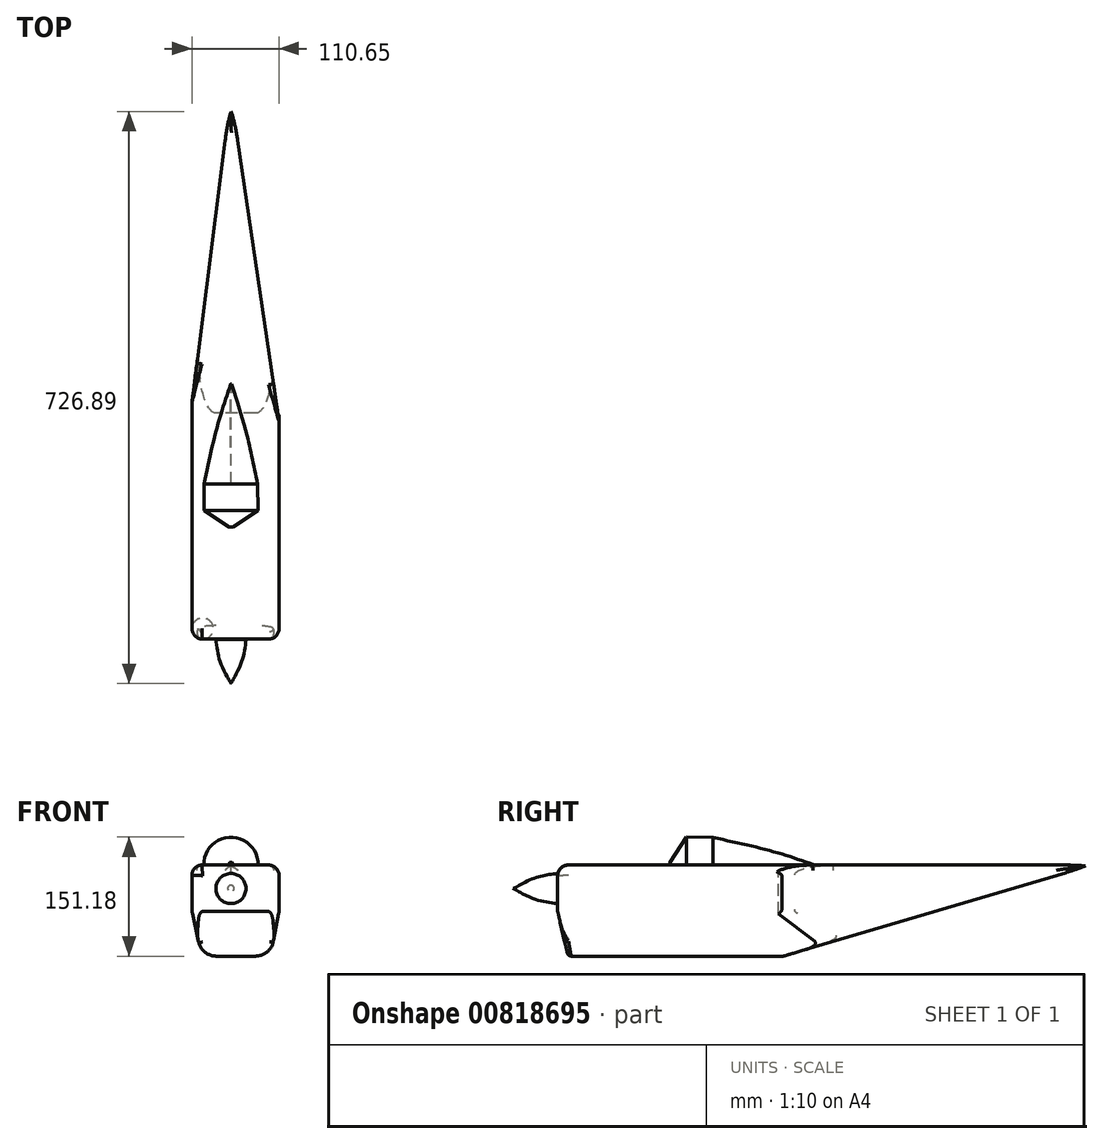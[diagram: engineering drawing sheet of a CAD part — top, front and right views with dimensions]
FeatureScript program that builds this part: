
annotation { "Feature Type Name" : "Feature", "Feature Type Description" : "" }
export const myFeature = defineFeature(function(context is Context, id is Id, definition is map)
    precondition{}
    {
        {
            var Q0;
            Q0=qCreatedBy(makeId("Front.planeOp"),FACE);
            var sketch = newSketch(context, id + "F0", { "sketchPlane" : qUnion([Q0])});
            skLineSegment(sketch, "E0.bottom", {"start": v(-36.8, 41.62) * mm, "end": v(48.49, 41.62) * mm});
            skPoint(sketch, "E1.visualSharp", {"position": v(-49.5, 41.62) * mm});
            skArc(sketch, "E1.filletArc", {"start": v(-36.8, 41.62) * mm, "mid": v(-45.78, 37.9) * mm, "end": v(-49.5, 28.92) * mm});
            skPoint(sketch, "E2.visualSharp", {"position": v(61.15, 41.62) * mm});
            skArc(sketch, "E2.filletArc", {"start": v(61.15, 29.9) * mm, "mid": v(57.11, 38.24) * mm, "end": v(48.49, 41.62) * mm});
            skLineSegment(sketch, "E3", {"start": v(-49.5, 28.92) * mm, "end": v(-49.5, -14.97) * mm});
            skLineSegment(sketch, "E4", {"start": v(61.15, 29.9) * mm, "end": v(61.15, -15.21) * mm});
            skLineSegment(sketch, "E5", {"start": v(-48.98, -19.8) * mm, "end": v(-41.15, -56.04) * mm});
            skLineSegment(sketch, "E6", {"start": v(-18.8, -74.07) * mm, "end": v(31.3, -74.07) * mm});
            skLineSegment(sketch, "E7", {"start": v(60.73, -19.56) * mm, "end": v(53.75, -55.56) * mm});
            skPoint(sketch, "E8.visualSharp", {"position": v(-49.5, -17.4) * mm});
            skArc(sketch, "E8.filletArc", {"start": v(-49.5, -14.97) * mm, "mid": v(-49.37, -17.4) * mm, "end": v(-48.98, -19.8) * mm});
            skPoint(sketch, "E9.visualSharp", {"position": v(61.15, -17.4) * mm});
            skArc(sketch, "E9.filletArc", {"start": v(60.73, -19.56) * mm, "mid": v(61.04, -17.4) * mm, "end": v(61.15, -15.21) * mm});
            skPoint(sketch, "E10.visualSharp", {"position": v(-37.26, -74.07) * mm});
            skArc(sketch, "E10.filletArc", {"start": v(-41.15, -56.04) * mm, "mid": v(-33.16, -69) * mm, "end": v(-18.8, -74.07) * mm});
            skPoint(sketch, "E11.visualSharp", {"position": v(50.16, -74.07) * mm});
            skArc(sketch, "E11.filletArc", {"start": v(31.3, -74.07) * mm, "mid": v(45.85, -68.85) * mm, "end": v(53.75, -55.56) * mm});
            skSolve(sketch);
        }
        {
            var Q0;
            Q0=makeQuery(id+"F0.imprint","IMPRINT",FACE,{"disambiguationData":[TD([[makeQuery(id+"F0.imprint","IMPRINT",EDGE,{"derivedFrom":sQuery(id+"F0.wireOp",EDGE,"E0.bottom")}),-1.0]])]});
            extrude(context, id + "F1", {"entities" : qUnion([Q0]), "depth" : 197.36 * mm, "offsetDistance" : 25.4 * mm});
        }
        {
            var Q0;
            Q0=qCreatedBy(makeId("Right.planeOp"),FACE);
            var sketch = newSketch(context, id + "F2", { "sketchPlane" : qUnion([Q0])});
            skLineSegment(sketch, "E12", {"start": v(-198.25, -13.52) * mm, "end": v(-183.44, -77.59) * mm});
            skLineSegment(sketch, "E13", {"start": v(-183.44, -77.59) * mm, "end": v(-211.91, -77.59) * mm});
            skLineSegment(sketch, "E14", {"start": v(-211.91, -77.59) * mm, "end": v(-198.25, -13.52) * mm});
            skSolve(sketch);
        }
        {
            var Q0;
            Q0 = qSketchRegion(id + "F2", true);
            extrude(context, id + "F3", {"entities" : qUnion([Q0]), "operationType" : NewBodyOperationType.REMOVE, "endBound" : BoundingType.SYMMETRIC, "oppositeDirection" : true, "depth" : 143.26 * mm, "offsetDistance" : 25.4 * mm});
        }
        {
            var Q0;
            Q0=makeQuery(id+"F1.opExtrude","CAP_EDGE",EDGE,{"disambiguationData":[OSD([sQuery(id+"F0.wireOp",EDGE,"E0.bottom")])],"isStart":false});
            var Q1;
            Q1=makeQuery(id+"F1.opExtrude","CAP_EDGE",EDGE,{"disambiguationData":[OSD([sQuery(id+"F0.wireOp",EDGE,"E1.filletArc")])],"isStart":false});
            fillet(context, id + "F4", {"entities" : qUnion([Q0, Q1]), "radius" : 13.5 * mm, "tangentPropagation" : true, "allowEdgeOverflow" : false});
        }
        {
            var Q0;
            Q0=makeQuery(id+"F1.opExtrude","CAP_EDGE",EDGE,{"disambiguationData":[OSD([sQuery(id+"F0.wireOp",EDGE,"E4")])],"isStart":false});
            fillet(context, id + "F5", {"entities" : qUnion([Q0]), "radius" : 13.5 * mm, "tangentPropagation" : true, "allowEdgeOverflow" : false});
        }
        {
            var Q0;
            Q0=makeQuery(id+"F3.boolean.opBoolean","INTERSECT",EDGE,{"derivedFrom":[makeQuery(id+"F1.opExtrude","SWEPT_FACE",FACE,{"disambiguationData":[OSD([sQuery(id+"F0.wireOp",EDGE,"E6")])]}),makeQuery(id+"F3.opExtrude","SWEPT_FACE",FACE,{"disambiguationData":[OSD([sQuery(id+"F2.wireOp",EDGE,"E12")])]})]});
            fillet(context, id + "F6", {"entities" : qUnion([Q0]), "radius" : 5.08 * mm, "tangentPropagation" : true, "allowEdgeOverflow" : false});
        }
        {
            var Q0;
            Q0=qCreatedBy(makeId("Right.planeOp"),FACE);
            var sketch = newSketch(context, id + "F7", { "sketchPlane" : qUnion([Q0])});
            skFitSpline(sketch, "E15", {"points": [v(-197.64, 30.82) * mm, v(-231.23, 23.4) * mm, v(-253.86, 11.73) * mm, v(-254.21, 11.73) * mm], "startDerivative": vector(-64.18, -7.39) * mm, "endDerivative": vector(-4.4, 1.73) * mm});
            skLineSegment(sketch, "E16", {"start": v(-253.86, 11.73) * mm, "end": v(-197.28, 11.73) * mm});
            skLineSegment(sketch, "E17", {"start": v(-197.28, 11.73) * mm, "end": v(-197.64, 30.82) * mm});
            skSolve(sketch);
        }
        {
            var Q0;
            {var subQ2=sQuery(id+"F7.wireOp",EDGE,"E16");Q0=makeQuery(id+"F7.imprint","IMPRINT",FACE,{"disambiguationData":[TD([[makeQuery(id+"F7.imprint","IMPRINT",EDGE,{"derivedFrom":subQ2}),1.0]])]});}
            var Q1;
            Q1=sQuery(id+"F7.wireOp",EDGE,"E16");
            revolve(context, id + "F8", {"operationType" : NewBodyOperationType.ADD, "surfaceOperationType" : NewSurfaceOperationType.NEW, "entities" : qUnion([Q0]), "axis" : qUnion([Q1]), "revolveType" : RevolveType.FULL});
        }
        {
            var Q0;
            Q0=qCreatedBy(makeId("Right.planeOp"),FACE);
            var sketch = newSketch(context, id + "F9", { "sketchPlane" : qUnion([Q0])});
            skFitSpline(sketch, "E18", {"points": [v(-230.36, 22.97) * mm, v(-230.36, 83.18) * mm, v(-212.3, 158.02) * mm, v(-213.16, 160.6) * mm], "startDerivative": vector(-15.1, 123.32) * mm, "endDerivative": vector(-14.55, 16.84) * mm});
            skLineSegment(sketch, "E19", {"start": v(-221.76, 21.25) * mm, "end": v(-200.25, 158.88) * mm});
            skSolve(sketch);
        }
        {
            var Q0;
            Q0=sQuery(id+"F9.wireOp",EDGE,"E18");
            var Q1;
            Q1=sQuery(id+"F9.wireOp",EDGE,"E19");
            revolve(context, id + "F10", {"bodyType" : ToolBodyType.SURFACE, "surfaceOperationType" : NewSurfaceOperationType.NEW, "surfaceEntities" : qUnion([Q0]), "axis" : qUnion([Q1]), "revolveType" : RevolveType.SYMMETRIC, "angle" : 64.7 * degree});
        }
        {
            var Q0;
            Q0=makeQuery(id+"F10.opRevolve","SWEPT_BODY",BODY,{"disambiguationData":[OSD([sQuery(id+"F9.wireOp",EDGE,"E18")])]});
            var Q1;
            Q1=makeQuery(id+"F8.opRevolve","SWEPT_FACE",FACE,{"disambiguationData":[OSD([sQuery(id+"F7.wireOp",EDGE,"E15")])]});
            circularPattern(context, id + "F11", {"entities" : qUnion([Q0]), "axis" : qUnion([Q1]), "angle" : 360 * degree, "instanceCount" : 3, "equalSpace" : true});
        }
        {
            var Q0;
            Q0=makeQuery(id+"F1.opExtrude","CAP_FACE",FACE,{"disambiguationData":[OSD([sQuery(id+"F0.wireOp",EDGE,"E0.bottom"),sQuery(id+"F0.wireOp",EDGE,"E1.filletArc"),sQuery(id+"F0.wireOp",EDGE,"E2.filletArc"),sQuery(id+"F0.wireOp",EDGE,"E3"),sQuery(id+"F0.wireOp",EDGE,"E4"),sQuery(id+"F0.wireOp",EDGE,"E5"),sQuery(id+"F0.wireOp",EDGE,"E6"),sQuery(id+"F0.wireOp",EDGE,"E7"),sQuery(id+"F0.wireOp",EDGE,"E8.filletArc"),sQuery(id+"F0.wireOp",EDGE,"E9.filletArc"),sQuery(id+"F0.wireOp",EDGE,"E10.filletArc"),sQuery(id+"F0.wireOp",EDGE,"E11.filletArc")])],"isStart":true});
            extrude(context, id + "F12", {"entities" : qUnion([Q0]), "operationType" : NewBodyOperationType.ADD, "depth" : 487.68 * mm, "offsetDistance" : 25.4 * mm});
        }
        {
            var Q0;
            Q0=qCreatedBy(makeId("Right.planeOp"),FACE);
            var sketch = newSketch(context, id + "F13", { "sketchPlane" : qUnion([Q0])});
            skLineSegment(sketch, "E20", {"start": v(487.34, 43.68) * mm, "end": v(84.62, -75.55) * mm});
            skLineSegment(sketch, "E21", {"start": v(84.62, -75.55) * mm, "end": v(96.3, -139.76) * mm});
            skLineSegment(sketch, "E22", {"start": v(-92.85, -139.76) * mm, "end": v(-114.72, -139.76) * mm});
            skLineSegment(sketch, "E23", {"start": v(96.3, -139.76) * mm, "end": v(500.84, -115.19) * mm});
            skLineSegment(sketch, "E24", {"start": v(508.98, -115.19) * mm, "end": v(508.98, 90.1) * mm});
            skLineSegment(sketch, "E25", {"start": v(487.34, 43.68) * mm, "end": v(508.98, 90.1) * mm});
            skLineSegment(sketch, "E26", {"start": v(508.98, 93.48) * mm, "end": v(500.84, -115.19) * mm});
            skLineSegment(sketch, "E27", {"start": v(508.98, -115.19) * mm, "end": v(500.84, -115.19) * mm});
            skSolve(sketch);
        }
        {
            var Q0;
            Q0 = qSketchRegion(id + "F13", true);
            extrude(context, id + "F14", {"entities" : qUnion([Q0]), "operationType" : NewBodyOperationType.REMOVE, "endBound" : BoundingType.SYMMETRIC, "depth" : 284.48 * mm, "offsetDistance" : 25.4 * mm});
        }
        {
            var Q0;
            Q0=qCreatedBy(makeId("Top.planeOp"),FACE);
            var sketch = newSketch(context, id + "F15", { "sketchPlane" : qUnion([Q0])});
            skLineSegment(sketch, "E28", {"start": v(-51.82, 85.84) * mm, "end": v(0, 494.02) * mm});
            skLineSegment(sketch, "E29", {"start": v(0, 494.02) * mm, "end": v(60.58, 82.88) * mm});
            skLineSegment(sketch, "E30", {"start": v(60.58, 82.88) * mm, "end": v(116.78, 511.76) * mm});
            skLineSegment(sketch, "E31", {"start": v(116.78, 511.76) * mm, "end": v(-122.8, 494.02) * mm});
            skLineSegment(sketch, "E32", {"start": v(-122.8, 494.02) * mm, "end": v(-51.82, 85.84) * mm});
            skSolve(sketch);
        }
        {
            var Q0;
            Q0 = qSketchRegion(id + "F15", true);
            extrude(context, id + "F16", {"entities" : qUnion([Q0]), "operationType" : NewBodyOperationType.REMOVE, "endBound" : BoundingType.SYMMETRIC, "oppositeDirection" : true, "depth" : 558.8 * mm, "offsetDistance" : 25.4 * mm});
        }
        {
            var Q0;
            {var subQ0=sQuery(id+"F0.wireOp",EDGE,"E0.bottom");Q0=makeQuery(id+"F16.boolean.opBoolean","INTERSECT",EDGE,{"derivedFrom":[makeQuery(id+"F12.boolean.opBoolean","MERGE",FACE,{"derivedFrom":[makeQuery(id+"F1.opExtrude","SWEPT_FACE",FACE,{"disambiguationData":[OSD([subQ0])]}),makeQuery(id+"F12.opExtrude","SWEPT_FACE",FACE,{"disambiguationData":[OSD([subQ0])]})]}),makeQuery(id+"F16.opExtrude","SWEPT_FACE",FACE,{"disambiguationData":[OSD([sQuery(id+"F15.wireOp",EDGE,"E28")])]})]});}
            var Q1;
            {var subQ0=sQuery(id+"F0.wireOp",EDGE,"E0.bottom");Q1=makeQuery(id+"F16.boolean.opBoolean","INTERSECT",EDGE,{"derivedFrom":[makeQuery(id+"F12.boolean.opBoolean","MERGE",FACE,{"derivedFrom":[makeQuery(id+"F1.opExtrude","SWEPT_FACE",FACE,{"disambiguationData":[OSD([subQ0])]}),makeQuery(id+"F12.opExtrude","SWEPT_FACE",FACE,{"disambiguationData":[OSD([subQ0])]})]}),makeQuery(id+"F16.opExtrude","SWEPT_FACE",FACE,{"disambiguationData":[OSD([sQuery(id+"F15.wireOp",EDGE,"E29")])]})]});}
            var Q2;
            Q2=makeQuery(id+"F16.boolean.opBoolean","INTERSECT",EDGE,{"derivedFrom":[makeQuery(id+"F14.boolean.opBoolean","COPY",FACE,{"derivedFrom":makeQuery(id+"F14.opExtrude","SWEPT_FACE",FACE,{"disambiguationData":[OSD([sQuery(id+"F13.wireOp",EDGE,"E20")])]})}),makeQuery(id+"F16.opExtrude","SWEPT_FACE",FACE,{"disambiguationData":[OSD([sQuery(id+"F15.wireOp",EDGE,"E29")])]})]});
            var Q3;
            Q3=makeQuery(id+"F16.boolean.opBoolean","INTERSECT",EDGE,{"derivedFrom":[makeQuery(id+"F14.boolean.opBoolean","COPY",FACE,{"derivedFrom":makeQuery(id+"F14.opExtrude","SWEPT_FACE",FACE,{"disambiguationData":[OSD([sQuery(id+"F13.wireOp",EDGE,"E20")])]})}),makeQuery(id+"F16.opExtrude","SWEPT_FACE",FACE,{"disambiguationData":[OSD([sQuery(id+"F15.wireOp",EDGE,"E28")])]})]});
            fillet(context, id + "F17", {"entities" : qUnion([Q0, Q1, Q2, Q3]), "radius" : 6.52 * mm, "tangentPropagation" : true, "allowEdgeOverflow" : false});
        }
        {
            var Q0;
            Q0=qCreatedBy(makeId("Right.planeOp"),FACE);
            var sketch = newSketch(context, id + "F18", { "sketchPlane" : qUnion([Q0])});
            skLineSegment(sketch, "E33", {"start": v(0, 76.6) * mm, "end": v(0, 42.6) * mm});
            skPoint(sketch, "E34.end.orphan", {"position": v(-54.87, 45.26) * mm});
            skPoint(sketch, "E35.start.orphan", {"position": v(-54.87, 42.76) * mm});
            skLineSegment(sketch, "E36", {"start": v(-54.87, 45.26) * mm, "end": v(-33.6, 77.11) * mm});
            skLineSegment(sketch, "E37", {"start": v(-33.6, 77.11) * mm, "end": v(0, 76.6) * mm});
            skLineSegment(sketch, "E38", {"start": v(0, 42.6) * mm, "end": v(-54.87, 42.76) * mm});
            skPoint(sketch, "E39.1.internal.snap0", {"position": v(0, 59.6) * mm});
            skFitSpline(sketch, "E39", {"points": [v(0, 76.6) * mm, v(73.55, 59.6) * mm, v(126.71, 42.76) * mm], "startDerivative": vector(142.4, -30.75) * mm, "endDerivative": vector(110.2, -35.41) * mm});
            skLineSegment(sketch, "E40", {"start": v(0, 42.6) * mm, "end": v(126.71, 42.76) * mm});
            skLineSegment(sketch, "E41", {"start": v(-54.87, 42.76) * mm, "end": v(-54.87, 45.26) * mm});
            skSolve(sketch);
        }
        {
            var Q0;
            Q0 = qSketchRegion(id + "F18", true);
            var Q1;
            Q1=sQuery(id+"F18.wireOp",EDGE,"E38");
            revolve(context, id + "F19", {"operationType" : NewBodyOperationType.ADD, "surfaceOperationType" : NewSurfaceOperationType.NEW, "entities" : qUnion([Q0]), "axis" : qUnion([Q1]), "revolveType" : RevolveType.FULL});
        }
    });
